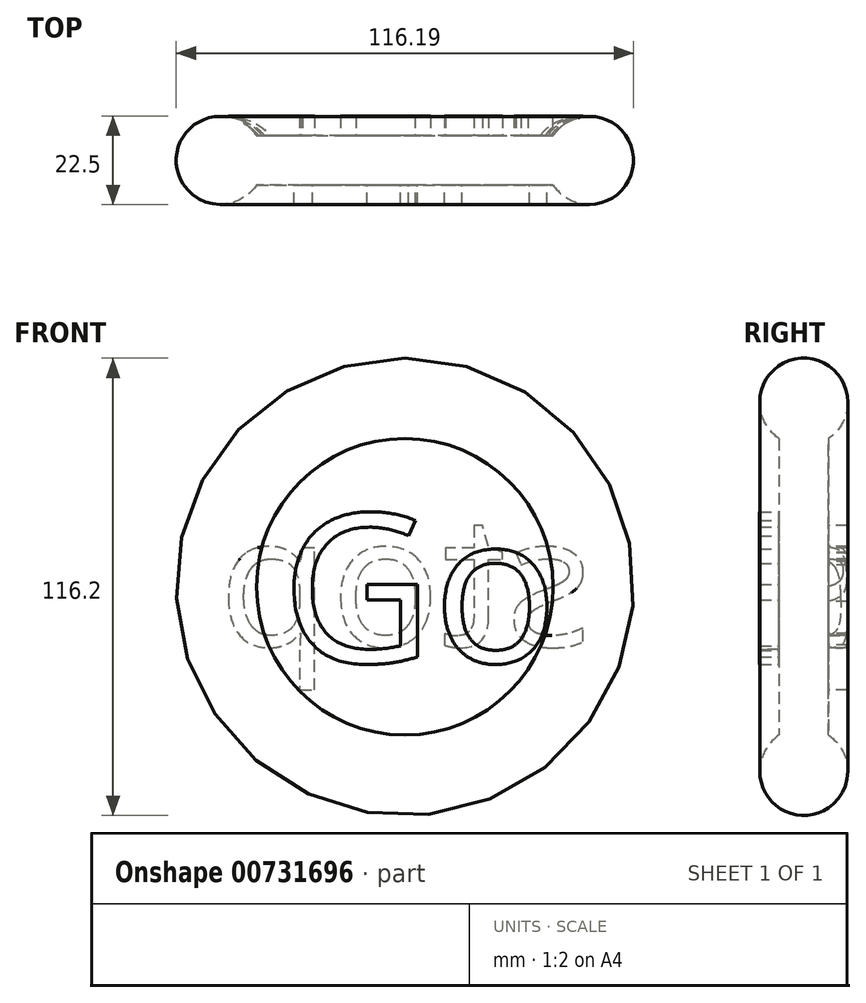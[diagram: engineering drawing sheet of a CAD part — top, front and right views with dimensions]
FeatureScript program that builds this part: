
annotation { "Feature Type Name" : "Feature", "Feature Type Description" : "" }
export const myFeature = defineFeature(function(context is Context, id is Id, definition is map)
    precondition{}
    {
        {
            var Q0;
            Q0=qCreatedBy(makeId("Top.planeOp"),FACE);
            var sketch = newSketch(context, id + "F0", { "sketchPlane" : qUnion([Q0])});
            skLineSegment(sketch, "E0.bottom", {"start": v(-42.4, 35.77) * mm, "end": v(12.98, 35.77) * mm});
            skLineSegment(sketch, "E0.top", {"start": v(-42.4, 23.27) * mm, "end": v(12.98, 23.27) * mm});
            skLineSegment(sketch, "E0.left", {"start": v(-42.4, 35.77) * mm, "end": v(-42.4, 23.27) * mm});
            skLineSegment(sketch, "E0.right", {"start": v(12.98, 35.77) * mm, "end": v(12.98, 23.27) * mm});
            skCircle(sketch, "E1", {"center": v(4.52, 29.52) * mm, "radius": 11.17 * mm});
            skPoint(sketch, "E1.centerSnap0", {"position": v(12.98, 29.52) * mm});
            skLineSegment(sketch, "E2", {"start": v(-48.42, 35.75) * mm, "end": v(-47.58, 22.1) * mm});
            skSolve(sketch);
        }
        {
            var Q0;
            {var subQ0=sQuery(id+"F0.wireOp",EDGE,"E0.left");Q0=makeQuery(id+"F0.imprint","IMPRINT",FACE,{"disambiguationData":[TD([[makeQuery(id+"F0.imprint","IMPRINT",EDGE,{"derivedFrom":subQ0}),1.0]])]});}
            var Q1;
            {var subQ0=sQuery(id+"F0.wireOp",EDGE,"E0.right");Q1=makeQuery(id+"F0.imprint","IMPRINT",FACE,{"disambiguationData":[TD([[makeQuery(id+"F0.imprint","IMPRINT",EDGE,{"derivedFrom":subQ0}),-1.0]])]});}
            var Q2;
            {var subQ0=sQuery(id+"F0.wireOp",EDGE,"E0.right");Q2=makeQuery(id+"F0.imprint","IMPRINT",FACE,{"disambiguationData":[TD([[makeQuery(id+"F0.imprint","IMPRINT",EDGE,{"derivedFrom":subQ0}),1.0]])]});}
            var Q3;
            Q3=sQuery(id+"F0.wireOp",EDGE,"E0.left");
            revolve(context, id + "F1", {"surfaceOperationType" : NewSurfaceOperationType.NEW, "entities" : qUnion([Q0, Q1, Q2]), "axis" : qUnion([Q3]), "revolveType" : RevolveType.FULL});
        }
        {
            var Q0;
            Q0=makeQuery(id+"F1.opRevolve","SWEPT_FACE",FACE,{"disambiguationData":[OSD([sQuery(id+"F0.wireOp",EDGE,"E0.bottom")])]});
            var sketch = newSketch(context, id + "F2", { "sketchPlane" : qUnion([Q0])});
            skText(sketch, "E3", { "text": "stop", "fontName": "OpenSans-Regular.ttf"});
            const initialGuessF2  = {"E3": [-0.0053, -0.01506, 1, 0, 0.03346]};
            skSetInitialGuess(sketch, initialGuessF2);
            skSolve(sketch);
        }
        {
            var Q0;
            Q0 = qSketchRegion(id + "F2", true);
            extrude(context, id + "F3", {"entities" : qUnion([Q0]), "operationType" : NewBodyOperationType.ADD, "depth" : 5 * mm, "offsetDistance" : 25 * mm});
        }
        {
            var Q0;
            Q0=makeQuery(id+"F1.opRevolve","SWEPT_FACE",FACE,{"disambiguationData":[OSD([sQuery(id+"F0.wireOp",EDGE,"E0.top")])]});
            var sketch = newSketch(context, id + "F4", { "sketchPlane" : qUnion([Q0])});
            skText(sketch, "E4", { "text": "Go", "fontName": "OpenSans-Regular.ttf"});
            const initialGuessF4  = {"E4": [-0.0738, -0.01923, 1, 0, 0.03808]};
            skSetInitialGuess(sketch, initialGuessF4);
            skSolve(sketch);
        }
        {
            var Q0;
            Q0 = qSketchRegion(id + "F4", true);
            extrude(context, id + "F5", {"entities" : qUnion([Q0]), "operationType" : NewBodyOperationType.ADD, "depth" : 5 * mm, "offsetDistance" : 25 * mm});
        }
    });
